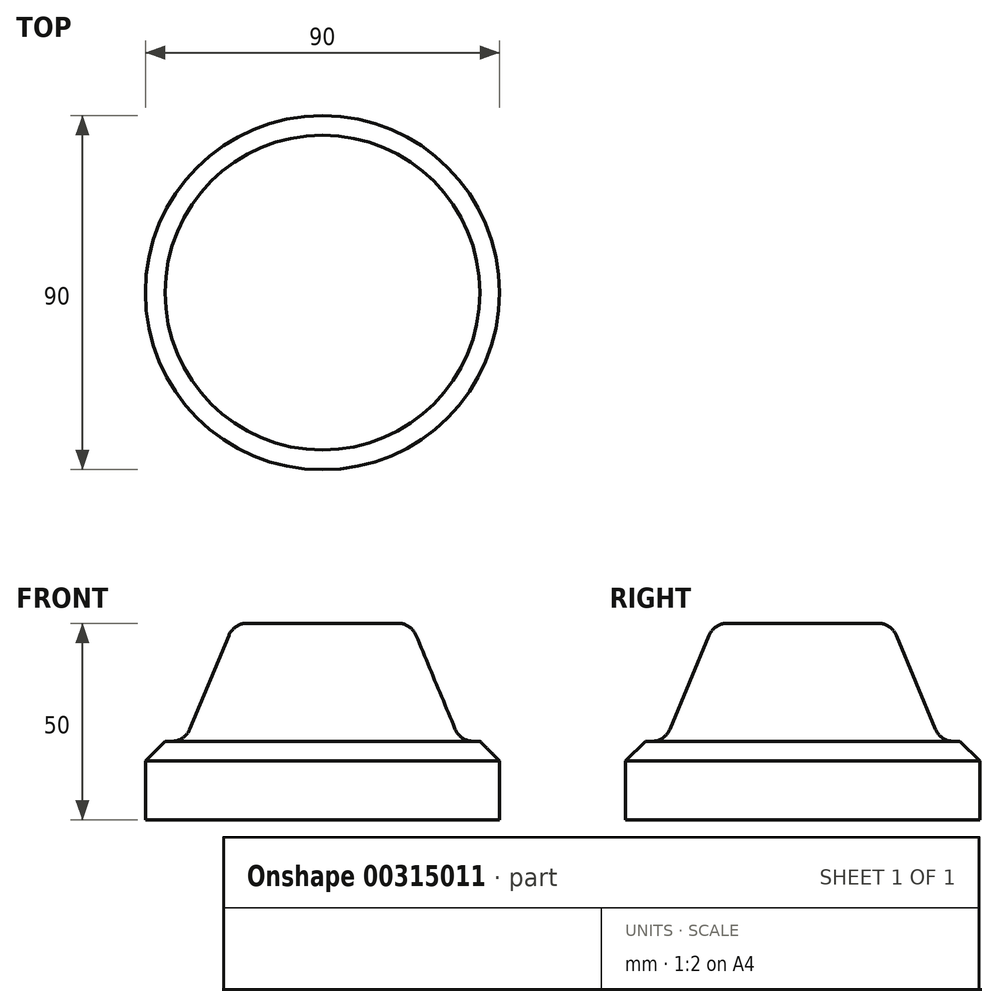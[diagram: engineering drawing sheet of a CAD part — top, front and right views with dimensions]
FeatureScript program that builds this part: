
annotation { "Feature Type Name" : "Feature", "Feature Type Description" : "" }
export const myFeature = defineFeature(function(context is Context, id is Id, definition is map)
    precondition{}
    {
        {
            var Q0;
            Q0=qCreatedBy(makeId("Front.planeOp"),FACE);
            var sketch = newSketch(context, id + "F0", { "sketchPlane" : qUnion([Q0])});
            skLineSegment(sketch, "E0", {"start": v(0, 0) * mm, "end": v(0, 50) * mm});
            skLineSegment(sketch, "E1", {"start": v(0, 50) * mm, "end": v(19.17, 50) * mm});
            skLineSegment(sketch, "E2", {"start": v(23.78, 46.92) * mm, "end": v(33.72, 23.08) * mm});
            skLineSegment(sketch, "E3", {"start": v(38.33, 20) * mm, "end": v(45, 20) * mm});
            skLineSegment(sketch, "E4", {"start": v(45, 20) * mm, "end": v(45, 0) * mm});
            skLineSegment(sketch, "E5", {"start": v(45, 0) * mm, "end": v(0, 0) * mm});
            skPoint(sketch, "E6.visualSharp", {"position": v(22.5, 50) * mm});
            skArc(sketch, "E6.filletArc", {"start": v(23.78, 46.92) * mm, "mid": v(21.94, 49.16) * mm, "end": v(19.17, 50) * mm});
            skPoint(sketch, "E7.visualSharp", {"position": v(35, 20) * mm});
            skArc(sketch, "E7.filletArc", {"start": v(33.72, 23.08) * mm, "mid": v(35.56, 20.84) * mm, "end": v(38.33, 20) * mm});
            skLineSegment(sketch, "E8", {"start": v(0, 62.28) * mm, "end": v(0, -16.33) * mm, "construction": true});
            skSolve(sketch);
        }
        {
            var Q0;
            Q0=makeQuery(id+"F0.imprint","IMPRINT",FACE,{"disambiguationData":[TD([[makeQuery(id+"F0.imprint","IMPRINT",EDGE,{"derivedFrom":sQuery(id+"F0.wireOp",EDGE,"E0")}),-1.0]])]});
            var Q1;
            Q1=sQuery(id+"F0.wireOp",EDGE,"E8");
            revolve(context, id + "F1", {"entities" : qUnion([Q0]), "axis" : qUnion([Q1]), "revolveType" : RevolveType.FULL});
        }
        {
            var Q0;
            Q0=makeQuery(id+"F1.opRevolve","SWEPT_EDGE",EDGE,{"disambiguationData":[OSD([sQuery(id+"F0.wireOp",EDGE,"E3"),sQuery(id+"F0.wireOp",EDGE,"E4")])]});
            var Q1;
            Q1=makeQuery(id+"F1.opRevolve","SWEPT_EDGE",EDGE,{"disambiguationData":[OSD([sQuery(id+"F0.wireOp",EDGE,"E2"),sQuery(id+"F0.wireOp",EDGE,"E7.filletArc")])]});
            var Q2;
            Q2=makeQuery(id+"F1.opRevolve","SWEPT_EDGE",EDGE,{"disambiguationData":[OSD([sQuery(id+"F0.wireOp",EDGE,"E2"),sQuery(id+"F0.wireOp",EDGE,"E6.filletArc")])]});
            var Q3;
            Q3=makeQuery(id+"F1.opRevolve","SWEPT_EDGE",EDGE,{"disambiguationData":[OSD([sQuery(id+"F0.wireOp",EDGE,"E1"),sQuery(id+"F0.wireOp",EDGE,"E6.filletArc")])]});
            chamfer(context, id + "F2", {"entities" : qUnion([Q0, Q1, Q2, Q3]), "width" : 5 * mm, "tangentPropagation" : true});
        }
    });
